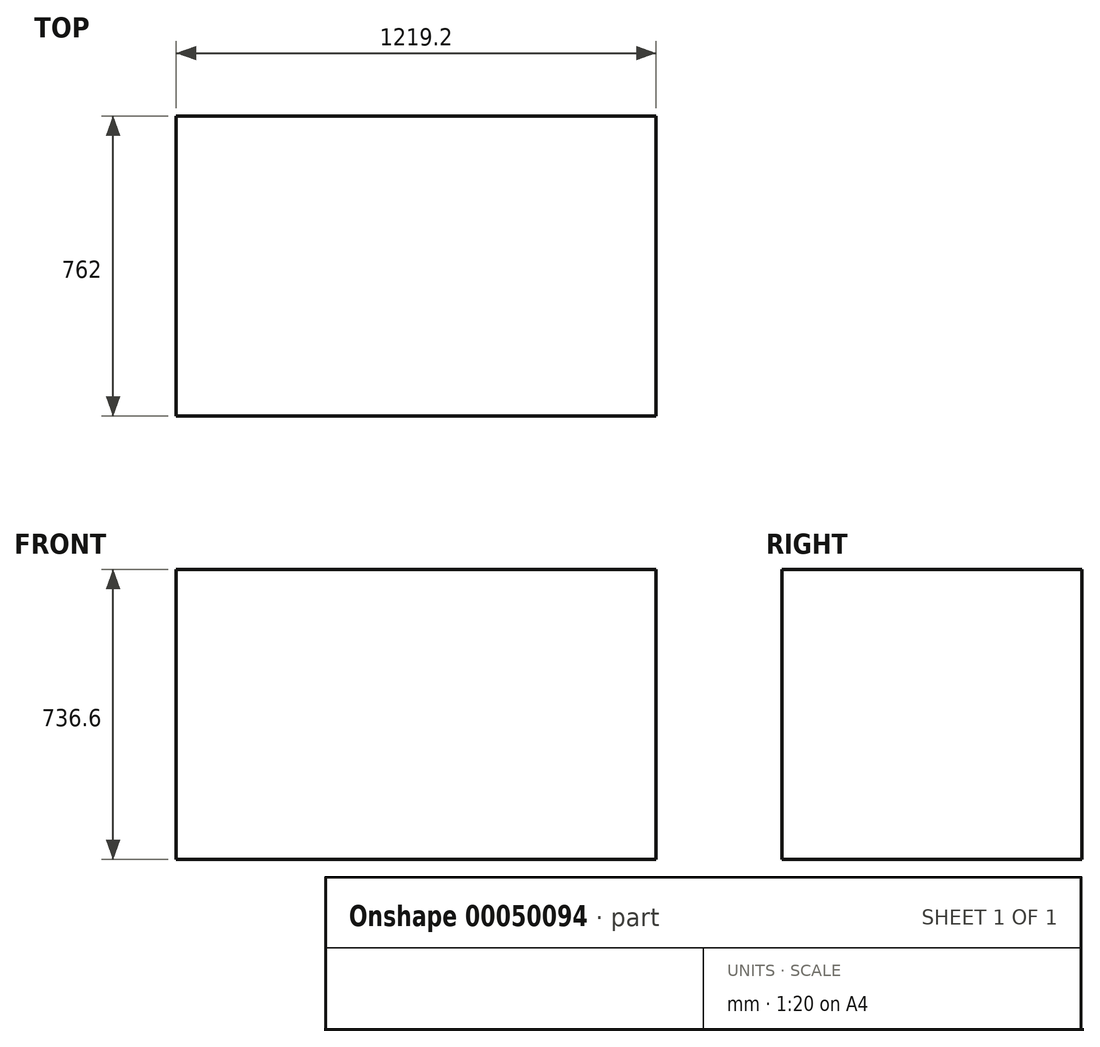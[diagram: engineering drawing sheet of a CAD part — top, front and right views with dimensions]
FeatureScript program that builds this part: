
annotation { "Feature Type Name" : "Feature", "Feature Type Description" : "" }
export const myFeature = defineFeature(function(context is Context, id is Id, definition is map)
    precondition{}
    {
        {
            var Q0;
            Q0=qCreatedBy(makeId("Top.planeOp"),FACE);
            var sketch = newSketch(context, id + "F0", { "sketchPlane" : qUnion([Q0])});
            skLineSegment(sketch, "E0.bottom", {"start": v(-609.6, 381) * mm, "end": v(609.6, 381) * mm});
            skLineSegment(sketch, "E0.top", {"start": v(-609.6, -381) * mm, "end": v(609.6, -381) * mm});
            skLineSegment(sketch, "E0.left", {"start": v(-609.6, 381) * mm, "end": v(-609.6, -381) * mm});
            skLineSegment(sketch, "E0.right", {"start": v(609.6, 381) * mm, "end": v(609.6, -381) * mm});
            skSolve(sketch);
        }
        {
            var Q0;
            Q0 = qSketchRegion(id + "F0", true);
            extrude(context, id + "F1", {"entities" : qUnion([Q0]), "depth" : 736.6 * mm});
        }
    });
